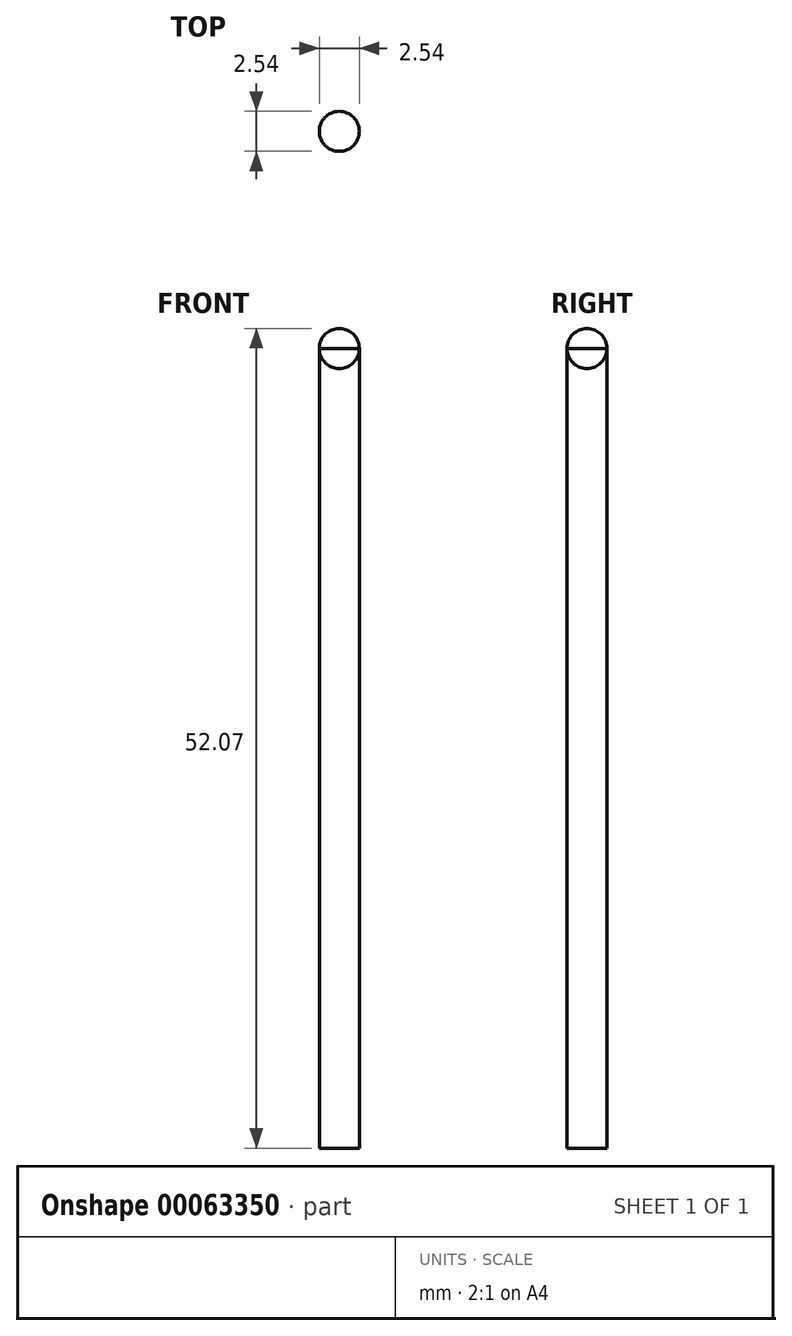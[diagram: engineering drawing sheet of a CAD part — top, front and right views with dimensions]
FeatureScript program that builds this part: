
annotation { "Feature Type Name" : "Feature", "Feature Type Description" : "" }
export const myFeature = defineFeature(function(context is Context, id is Id, definition is map)
    precondition{}
    {
        {
            var Q0;
            Q0=qCreatedBy(makeId("Top.planeOp"),FACE);
            var sketch = newSketch(context, id + "F0", { "sketchPlane" : qUnion([Q0])});
            skCircle(sketch, "E0", {"center": v(0, 0) * mm, "radius": 1.27 * mm});
            skSolve(sketch);
        }
        {
            var Q0;
            Q0=makeQuery(id+"F0.imprint","IMPRINT",FACE,{"disambiguationData":[TD([[makeQuery(id+"F0.imprint","IMPRINT",EDGE,{"derivedFrom":sQuery(id+"F0.wireOp",EDGE,"E0")}),1.0]])]});
            extrude(context, id + "F1", {"entities" : qUnion([Q0]), "endBound" : BoundingType.SYMMETRIC, "depth" : 50.8 * mm});
        }
        {
            var Q0;
            Q0=makeQuery(id+"F1.opExtrude","CAP_FACE",FACE,{"disambiguationData":[OSD([sQuery(id+"F0.wireOp",EDGE,"E0")])],"isStart":false});
            var sketch = newSketch(context, id + "F2", { "sketchPlane" : qUnion([Q0])});
            skCircle(sketch, "E1.0.0", {"center": v(0, 0) * mm, "radius": 1.27 * mm});
            skLineSegment(sketch, "E2", {"start": v(-1.27, 0) * mm, "end": v(1.27, 0) * mm});
            skLineSegment(sketch, "E3", {"start": v(0, 1.27) * mm, "end": v(0, -1.27) * mm});
            skSolve(sketch);
        }
        {
            var Q0;
            {var subQ0=sQuery(id+"F2.wireOp",EDGE,"E2");var subQ1=sQuery(id+"F2.wireOp",EDGE,"E1.0.0");var subQ2=makeQuery(id+"F2.imprint","INTERSECT",VERTEX,{"disambiguationData":[OD(1.0)],"derivedFrom":[subQ1,subQ0]});Q0=makeQuery(id+"F2.imprint","IMPRINT",FACE,{"disambiguationData":[TD([[makeQuery(id+"F2.imprint","IMPRINT",EDGE,{"disambiguationData":[TD([[subQ2,-1.0]])],"derivedFrom":subQ1}),1.0]])]});}
            var Q1;
            {var subQ0=sQuery(id+"F2.wireOp",EDGE,"E2");var subQ1=sQuery(id+"F2.wireOp",EDGE,"E1.0.0");var subQ2=makeQuery(id+"F2.imprint","INTERSECT",VERTEX,{"disambiguationData":[OD(1.0)],"derivedFrom":[subQ1,subQ0]});Q1=makeQuery(id+"F2.imprint","IMPRINT",FACE,{"disambiguationData":[TD([[makeQuery(id+"F2.imprint","IMPRINT",EDGE,{"disambiguationData":[TD([[subQ2,1.0]])],"derivedFrom":subQ1}),1.0]])]});}
            var Q2;
            Q2=sQuery(id+"F2.wireOp",EDGE,"E3");
            revolve(context, id + "F3", {"entities" : qUnion([Q0, Q1]), "axis" : qUnion([Q2]), "revolveType" : RevolveType.FULL});
        }
    });
